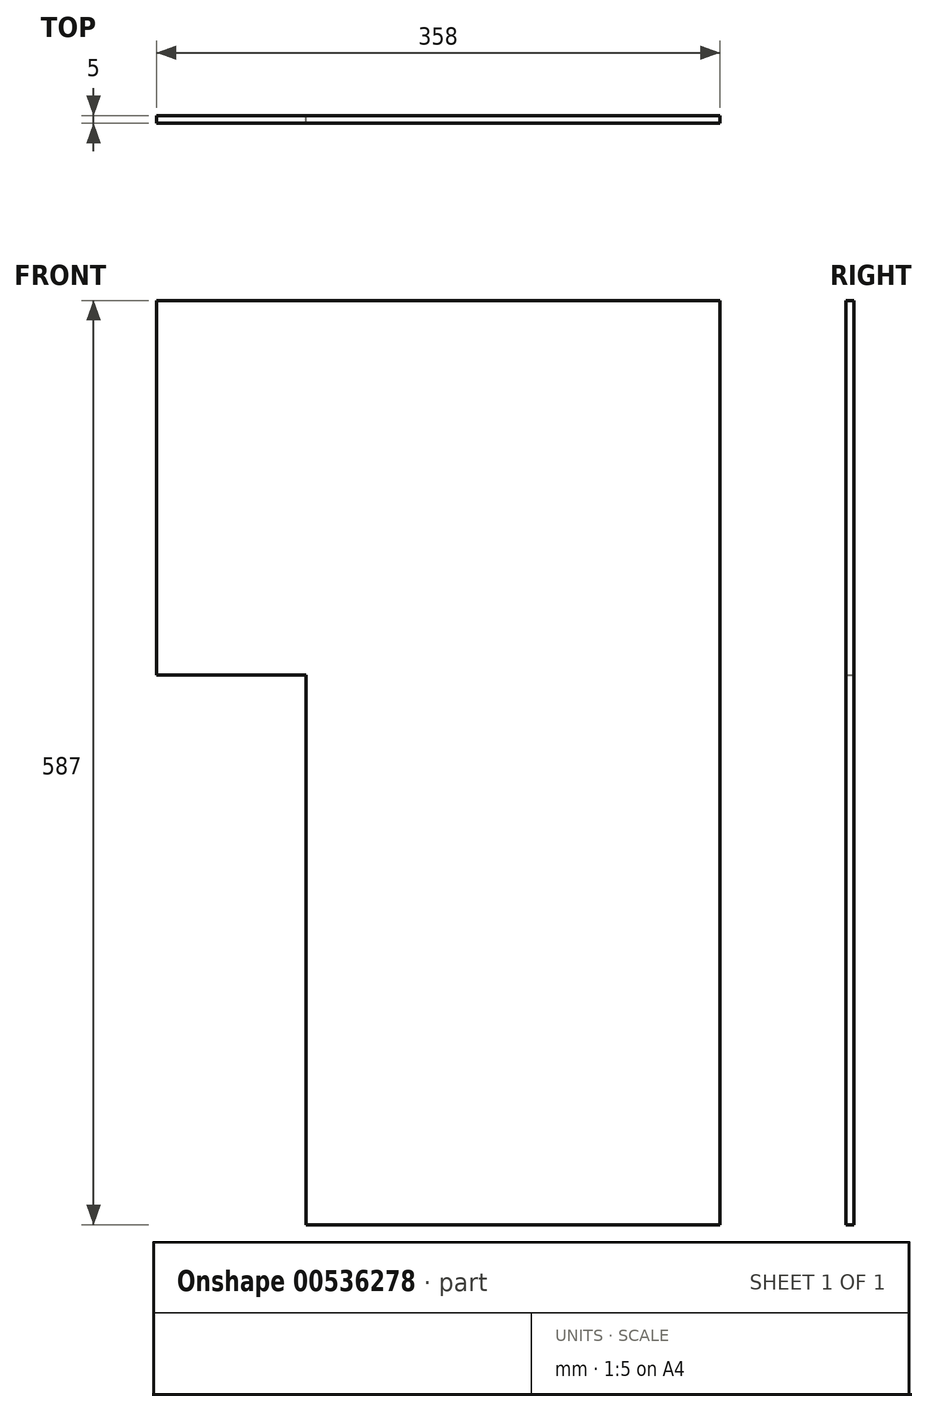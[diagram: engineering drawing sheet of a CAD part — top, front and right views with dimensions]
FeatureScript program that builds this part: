
annotation { "Feature Type Name" : "Feature", "Feature Type Description" : "" }
export const myFeature = defineFeature(function(context is Context, id is Id, definition is map)
    precondition{}
    {
        {
            var Q0;
            Q0=qCreatedBy(makeId("Front.planeOp"),FACE);
            var sketch = newSketch(context, id + "F0", { "sketchPlane" : qUnion([Q0])});
            skLineSegment(sketch, "E0", {"start": v(-84, 0) * mm, "end": v(-84, -349) * mm});
            skLineSegment(sketch, "E1", {"start": v(-84, -349) * mm, "end": v(179, -349) * mm});
            skLineSegment(sketch, "E2", {"start": v(179, -349) * mm, "end": v(179, 238) * mm});
            skLineSegment(sketch, "E3", {"start": v(179, 238) * mm, "end": v(-179, 238) * mm});
            skLineSegment(sketch, "E4", {"start": v(-179, 238) * mm, "end": v(-179, 0) * mm});
            skLineSegment(sketch, "E5", {"start": v(-179, 0) * mm, "end": v(-84, 0) * mm});
            skSolve(sketch);
        }
        {
            var Q0;
            Q0=makeQuery(id+"F0.imprint","IMPRINT",FACE,{"disambiguationData":[TD([[makeQuery(id+"F0.imprint","IMPRINT",EDGE,{"derivedFrom":sQuery(id+"F0.wireOp",EDGE,"E0")}),1.0]])]});
            extrude(context, id + "F1", {"entities" : qUnion([Q0]), "depth" : 5 * mm, "offsetDistance" : 25 * mm});
        }
    });
